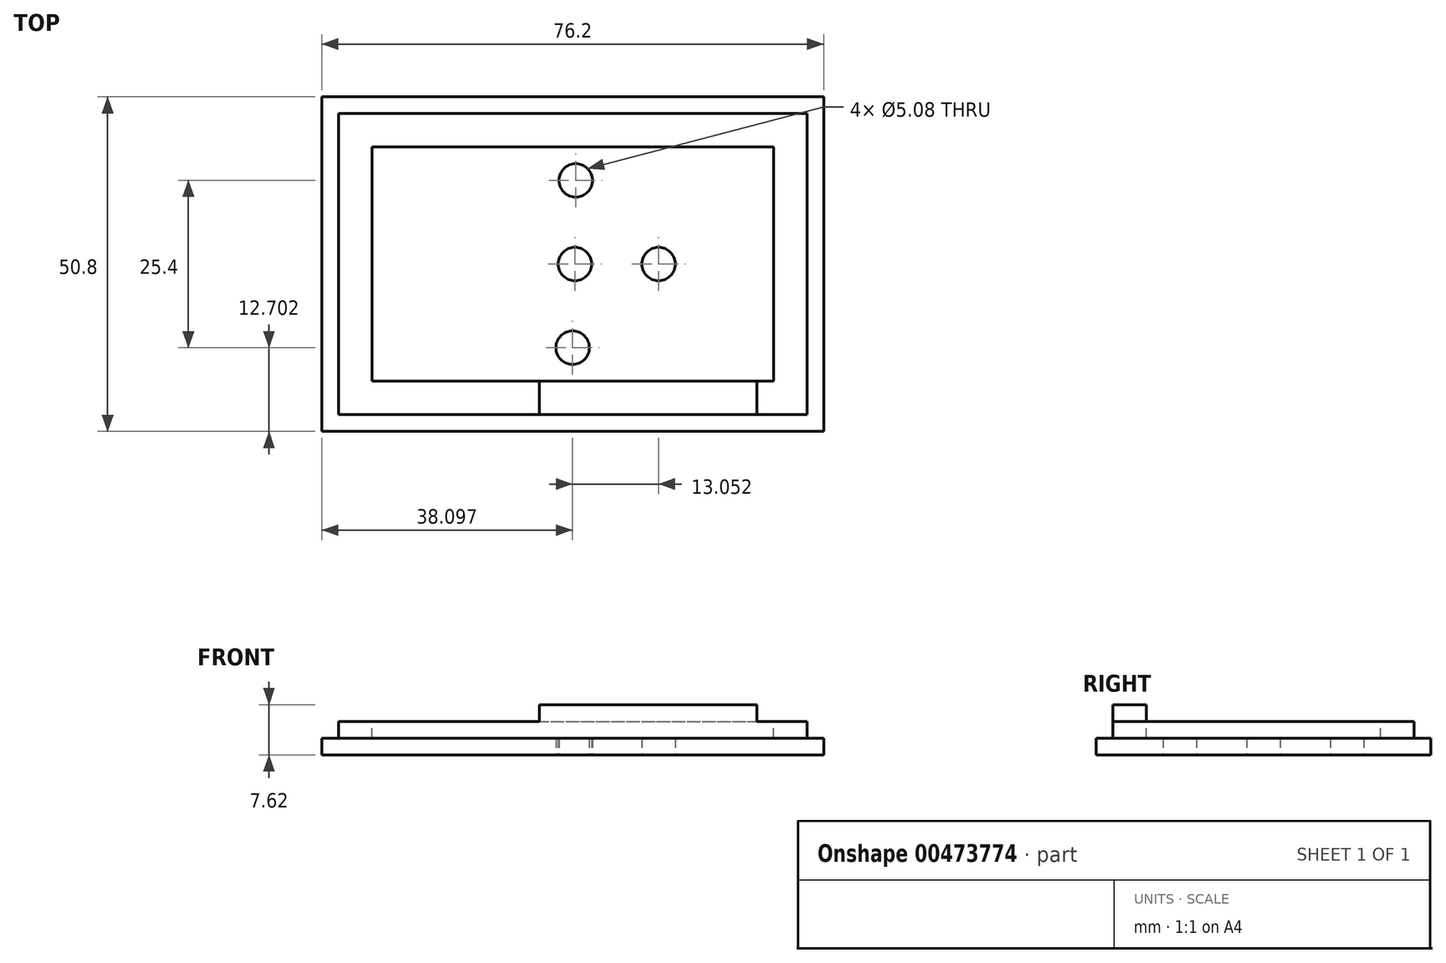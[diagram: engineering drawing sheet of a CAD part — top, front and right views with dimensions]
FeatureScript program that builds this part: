
annotation { "Feature Type Name" : "Feature", "Feature Type Description" : "" }
export const myFeature = defineFeature(function(context is Context, id is Id, definition is map)
    precondition{}
    {
        {
            var Q0;
            Q0=qCreatedBy(makeId("Top.planeOp"),FACE);
            var sketch = newSketch(context, id + "F0", { "sketchPlane" : qUnion([Q0])});
            skLineSegment(sketch, "E0.bottom", {"start": v(-24.47, 24.33) * mm, "end": v(51.73, 24.33) * mm});
            skLineSegment(sketch, "E0.top", {"start": v(-24.47, -26.47) * mm, "end": v(51.73, -26.47) * mm});
            skLineSegment(sketch, "E0.left", {"start": v(-24.47, 24.33) * mm, "end": v(-24.47, -26.47) * mm});
            skLineSegment(sketch, "E0.right", {"start": v(51.73, 24.33) * mm, "end": v(51.73, -26.47) * mm});
            skSolve(sketch);
        }
        {
            var Q0;
            Q0 = qSketchRegion(id + "F0", true);
            extrude(context, id + "F1", {"entities" : qUnion([Q0]), "depth" : 2.54 * mm});
        }
        {
            var Q0;
            Q0=makeQuery(id+"F1.opExtrude","CAP_FACE",FACE,{"disambiguationData":[OSD([sQuery(id+"F0.wireOp",EDGE,"E0.bottom"),sQuery(id+"F0.wireOp",EDGE,"E0.top"),sQuery(id+"F0.wireOp",EDGE,"E0.left"),sQuery(id+"F0.wireOp",EDGE,"E0.right")])],"isStart":false});
            var sketch = newSketch(context, id + "F2", { "sketchPlane" : qUnion([Q0])});
            skLineSegment(sketch, "E1.bottom", {"start": v(-21.93, 21.8) * mm, "end": v(49.19, 21.8) * mm});
            skLineSegment(sketch, "E1.top", {"start": v(-21.93, -23.93) * mm, "end": v(49.19, -23.93) * mm});
            skLineSegment(sketch, "E1.left", {"start": v(-21.93, 21.8) * mm, "end": v(-21.93, -23.93) * mm});
            skLineSegment(sketch, "E1.right", {"start": v(49.19, 21.8) * mm, "end": v(49.19, -23.93) * mm});
            skLineSegment(sketch, "E2", {"start": v(49.19, -23.93) * mm, "end": v(51.73, -23.93) * mm});
            skLineSegment(sketch, "E3", {"start": v(-21.93, -23.93) * mm, "end": v(-21.93, -26.47) * mm});
            skSolve(sketch);
        }
        {
            var Q0;
            Q0=makeQuery(id+"F2.imprint","IMPRINT",FACE,{"disambiguationData":[TD([[makeQuery(id+"F2.imprint","IMPRINT",EDGE,{"derivedFrom":sQuery(id+"F2.wireOp",EDGE,"E1.bottom")}),-1.0]])]});
            extrude(context, id + "F3", {"entities" : qUnion([Q0]), "operationType" : NewBodyOperationType.ADD, "depth" : 2.54 * mm});
        }
        {
            var Q0;
            Q0=makeQuery(id+"F3.opExtrude","CAP_FACE",FACE,{"disambiguationData":[OSD([sQuery(id+"F2.wireOp",EDGE,"E1.bottom"),sQuery(id+"F2.wireOp",EDGE,"E1.top"),sQuery(id+"F2.wireOp",EDGE,"E1.left"),sQuery(id+"F2.wireOp",EDGE,"E1.right")])],"isStart":false});
            var sketch = newSketch(context, id + "F4", { "sketchPlane" : qUnion([Q0])});
            skLineSegment(sketch, "E4.bottom", {"start": v(8.55, -18.85) * mm, "end": v(41.57, -18.85) * mm});
            skLineSegment(sketch, "E4.top", {"start": v(8.55, -23.93) * mm, "end": v(41.57, -23.93) * mm});
            skLineSegment(sketch, "E4.left", {"start": v(8.55, -18.85) * mm, "end": v(8.55, -23.93) * mm});
            skLineSegment(sketch, "E4.right", {"start": v(41.57, -18.85) * mm, "end": v(41.57, -23.93) * mm});
            skLineSegment(sketch, "E5", {"start": v(-21.93, -23.93) * mm, "end": v(8.55, -23.93) * mm});
            skSolve(sketch);
        }
        {
            var Q0;
            Q0=makeQuery(id+"F4.imprint","IMPRINT",FACE,{"disambiguationData":[TD([[makeQuery(id+"F4.imprint","IMPRINT",EDGE,{"derivedFrom":sQuery(id+"F4.wireOp",EDGE,"E4.bottom")}),-1.0]])]});
            extrude(context, id + "F5", {"entities" : qUnion([Q0]), "operationType" : NewBodyOperationType.ADD, "depth" : 2.54 * mm});
        }
        {
            var Q0;
            Q0=makeQuery(id+"F3.opExtrude","CAP_FACE",FACE,{"disambiguationData":[OSD([sQuery(id+"F2.wireOp",EDGE,"E1.bottom"),sQuery(id+"F2.wireOp",EDGE,"E1.top"),sQuery(id+"F2.wireOp",EDGE,"E1.left"),sQuery(id+"F2.wireOp",EDGE,"E1.right")])],"isStart":false});
            var sketch = newSketch(context, id + "F6", { "sketchPlane" : qUnion([Q0])});
            skLineSegment(sketch, "E6.bottom", {"start": v(-16.85, 16.71) * mm, "end": v(44.1, 16.71) * mm});
            skLineSegment(sketch, "E6.top", {"start": v(-16.85, -18.85) * mm, "end": v(44.1, -18.85) * mm});
            skLineSegment(sketch, "E6.left", {"start": v(-16.85, 16.71) * mm, "end": v(-16.85, -18.85) * mm});
            skLineSegment(sketch, "E6.right", {"start": v(44.1, 16.71) * mm, "end": v(44.1, -18.85) * mm});
            skLineSegment(sketch, "E7", {"start": v(-16.85, -18.85) * mm, "end": v(-21.93, -18.85) * mm});
            skSolve(sketch);
        }
        {
            var Q0;
            Q0=makeQuery(id+"F6.imprint","IMPRINT",FACE,{"disambiguationData":[TD([[makeQuery(id+"F6.imprint","IMPRINT",EDGE,{"derivedFrom":sQuery(id+"F6.wireOp",EDGE,"E6.bottom")}),-1.0]])]});
            extrude(context, id + "F7", {"entities" : qUnion([Q0]), "operationType" : NewBodyOperationType.REMOVE, "oppositeDirection" : true, "depth" : 2.54 * mm});
        }
        {
            var Q0;
            Q0=makeQuery(id+"F1.opExtrude","CAP_FACE",FACE,{"disambiguationData":[OSD([sQuery(id+"F0.wireOp",EDGE,"E0.bottom"),sQuery(id+"F0.wireOp",EDGE,"E0.top"),sQuery(id+"F0.wireOp",EDGE,"E0.left"),sQuery(id+"F0.wireOp",EDGE,"E0.right")])],"isStart":true});
            var sketch = newSketch(context, id + "F8", { "sketchPlane" : qUnion([Q0])});
            skCircle(sketch, "E8", {"center": v(13.63, 13.77) * mm, "radius": 2.54 * mm});
            skLineSegment(sketch, "E9", {"start": v(13.63, 13.77) * mm, "end": v(-24.47, 13.77) * mm});
            skLineSegment(sketch, "E10", {"start": v(13.63, 13.77) * mm, "end": v(13.63, 26.47) * mm});
            skCircle(sketch, "E11", {"center": v(13.98, 1.07) * mm, "radius": 2.54 * mm});
            skCircle(sketch, "E12", {"center": v(14.1, -11.63) * mm, "radius": 2.54 * mm});
            skLineSegment(sketch, "E13", {"start": v(14.1, -11.63) * mm, "end": v(14.1, -24.33) * mm});
            skLineSegment(sketch, "E14", {"start": v(14.1, -24.33) * mm, "end": v(13.98, 1.07) * mm});
            skCircle(sketch, "E15", {"center": v(26.68, 1.07) * mm, "radius": 2.54 * mm});
            skLineSegment(sketch, "E16", {"start": v(13.98, 1.07) * mm, "end": v(26.68, 1.07) * mm});
            skLineSegment(sketch, "E17", {"start": v(26.68, 1.07) * mm, "end": v(26.8, -24.33) * mm});
            skSolve(sketch);
        }
        {
            var Q0;
            {var subQ0=sQuery(id+"F8.wireOp",EDGE,"E9");var subQ1=sQuery(id+"F8.wireOp",EDGE,"E8");var subQ2=makeQuery(id+"F8.imprint","INTERSECT",VERTEX,{"derivedFrom":[subQ1,subQ0]});Q0=makeQuery(id+"F8.imprint","IMPRINT",FACE,{"disambiguationData":[TD([[makeQuery(id+"F8.imprint","IMPRINT",EDGE,{"disambiguationData":[TD([[subQ2,-1.0]])],"derivedFrom":subQ1}),1.0]])]});}
            var Q1;
            {var subQ0=sQuery(id+"F8.wireOp",EDGE,"E9");var subQ1=sQuery(id+"F8.wireOp",EDGE,"E8");var subQ2=makeQuery(id+"F8.imprint","INTERSECT",VERTEX,{"derivedFrom":[subQ1,subQ0]});Q1=makeQuery(id+"F8.imprint","IMPRINT",FACE,{"disambiguationData":[TD([[makeQuery(id+"F8.imprint","IMPRINT",EDGE,{"disambiguationData":[TD([[subQ2,1.0]])],"derivedFrom":subQ1}),1.0]])]});}
            var Q2;
            {var subQ0=sQuery(id+"F8.wireOp",EDGE,"E14");var subQ1=sQuery(id+"F8.wireOp",EDGE,"E11");var subQ2=makeQuery(id+"F8.imprint","INTERSECT",VERTEX,{"derivedFrom":[subQ1,subQ0]});Q2=makeQuery(id+"F8.imprint","IMPRINT",FACE,{"disambiguationData":[TD([[makeQuery(id+"F8.imprint","IMPRINT",EDGE,{"disambiguationData":[TD([[subQ2,1.0]])],"derivedFrom":subQ1}),1.0]])]});}
            var Q3;
            {var subQ0=sQuery(id+"F8.wireOp",EDGE,"E14");var subQ1=sQuery(id+"F8.wireOp",EDGE,"E11");var subQ2=makeQuery(id+"F8.imprint","INTERSECT",VERTEX,{"derivedFrom":[subQ1,subQ0]});Q3=makeQuery(id+"F8.imprint","IMPRINT",FACE,{"disambiguationData":[TD([[makeQuery(id+"F8.imprint","IMPRINT",EDGE,{"disambiguationData":[TD([[subQ2,-1.0]])],"derivedFrom":subQ1}),1.0]])]});}
            var Q4;
            {var subQ0=sQuery(id+"F8.wireOp",EDGE,"E12");var subQ1=makeQuery(id+"F8.imprint","INTERSECT",VERTEX,{"derivedFrom":[subQ0,sQuery(id+"F8.wireOp",EDGE,"E13")]});Q4=makeQuery(id+"F8.imprint","IMPRINT",FACE,{"disambiguationData":[TD([[makeQuery(id+"F8.imprint","IMPRINT",EDGE,{"disambiguationData":[TD([[subQ1,1.0]])],"derivedFrom":subQ0}),1.0]])]});}
            var Q5;
            {var subQ0=sQuery(id+"F8.wireOp",EDGE,"E14");var subQ1=sQuery(id+"F8.wireOp",EDGE,"E12");var subQ2=makeQuery(id+"F8.imprint","INTERSECT",VERTEX,{"disambiguationData":[OD(0.0)],"derivedFrom":[subQ1,subQ0]});Q5=makeQuery(id+"F8.imprint","IMPRINT",FACE,{"disambiguationData":[TD([[makeQuery(id+"F8.imprint","IMPRINT",EDGE,{"disambiguationData":[TD([[subQ2,1.0]])],"derivedFrom":subQ1}),1.0]])]});}
            var Q6;
            {var subQ0=sQuery(id+"F8.wireOp",EDGE,"E16");var subQ1=sQuery(id+"F8.wireOp",EDGE,"E15");var subQ2=makeQuery(id+"F8.imprint","INTERSECT",VERTEX,{"derivedFrom":[subQ1,subQ0]});Q6=makeQuery(id+"F8.imprint","IMPRINT",FACE,{"disambiguationData":[TD([[makeQuery(id+"F8.imprint","IMPRINT",EDGE,{"disambiguationData":[TD([[subQ2,-1.0]])],"derivedFrom":subQ1}),1.0]])]});}
            var Q7;
            {var subQ0=sQuery(id+"F8.wireOp",EDGE,"E16");var subQ1=sQuery(id+"F8.wireOp",EDGE,"E15");var subQ2=makeQuery(id+"F8.imprint","INTERSECT",VERTEX,{"derivedFrom":[subQ1,subQ0]});Q7=makeQuery(id+"F8.imprint","IMPRINT",FACE,{"disambiguationData":[TD([[makeQuery(id+"F8.imprint","IMPRINT",EDGE,{"disambiguationData":[TD([[subQ2,1.0]])],"derivedFrom":subQ1}),1.0]])]});}
            extrude(context, id + "F9", {"entities" : qUnion([Q0, Q1, Q2, Q3, Q4, Q5, Q6, Q7]), "operationType" : NewBodyOperationType.REMOVE, "oppositeDirection" : true, "depth" : 25.4 * mm});
        }
    });
